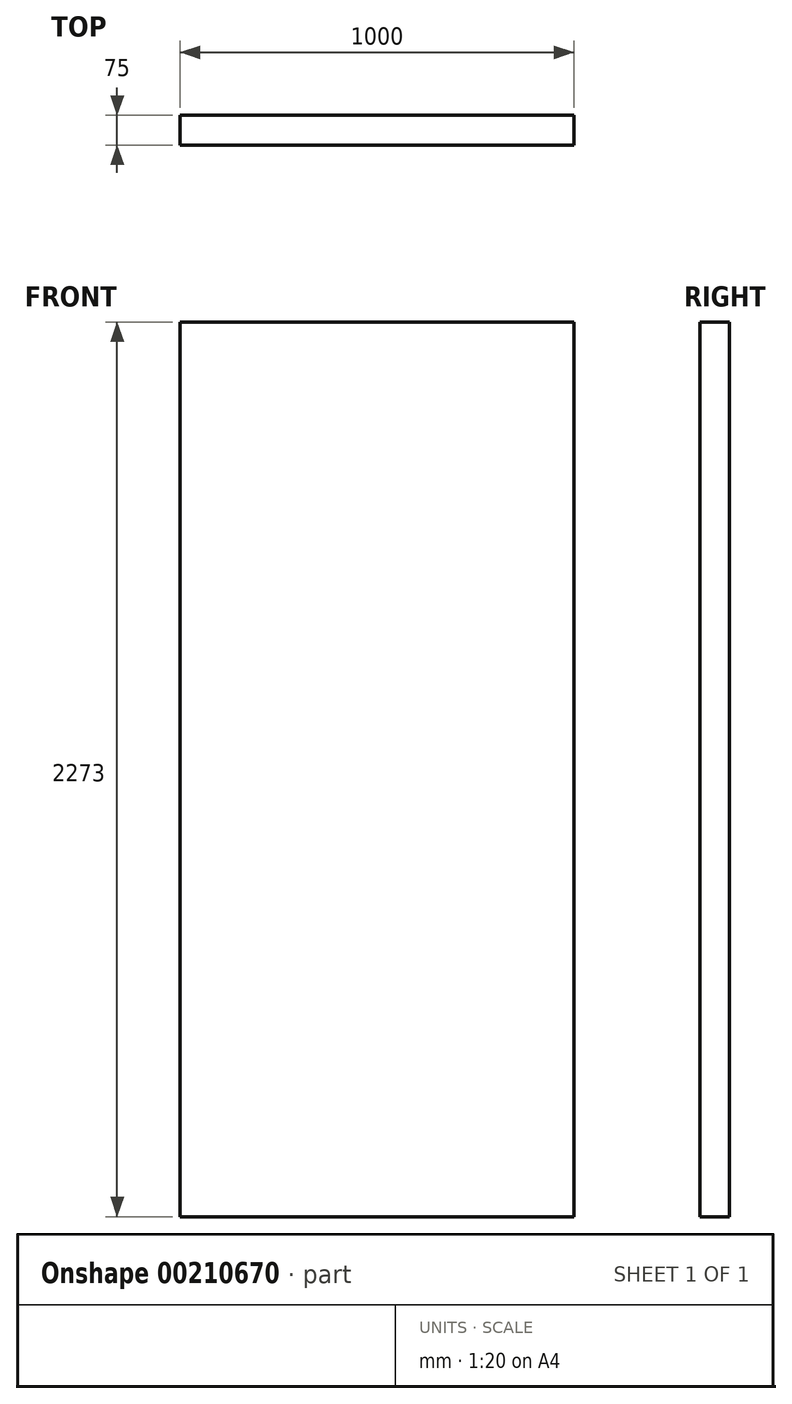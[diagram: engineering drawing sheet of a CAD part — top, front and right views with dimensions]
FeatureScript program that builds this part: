
annotation { "Feature Type Name" : "Feature", "Feature Type Description" : "" }
export const myFeature = defineFeature(function(context is Context, id is Id, definition is map)
    precondition{}
    {
        {
            var Q0;
            Q0=qCreatedBy(makeId("Front.planeOp"),FACE);
            var sketch = newSketch(context, id + "F0", { "sketchPlane" : qUnion([Q0])});
            skLineSegment(sketch, "E0.bottom", {"start": v(0, 0) * mm, "end": v(1000, 0) * mm});
            skLineSegment(sketch, "E0.top", {"start": v(0, 2273) * mm, "end": v(1000, 2273) * mm});
            skLineSegment(sketch, "E0.left", {"start": v(0, 0) * mm, "end": v(0, 2273) * mm});
            skLineSegment(sketch, "E0.right", {"start": v(1000, 0) * mm, "end": v(1000, 2273) * mm});
            skSolve(sketch);
        }
        {
            var Q0;
            Q0=makeQuery(id+"F0.imprint","IMPRINT",FACE,{"disambiguationData":[TD([[makeQuery(id+"F0.imprint","IMPRINT",EDGE,{"derivedFrom":sQuery(id+"F0.wireOp",EDGE,"E0.bottom")}),1.0]])]});
            extrude(context, id + "F1", {"entities" : qUnion([Q0]), "depth" : 75 * mm});
        }
    });
